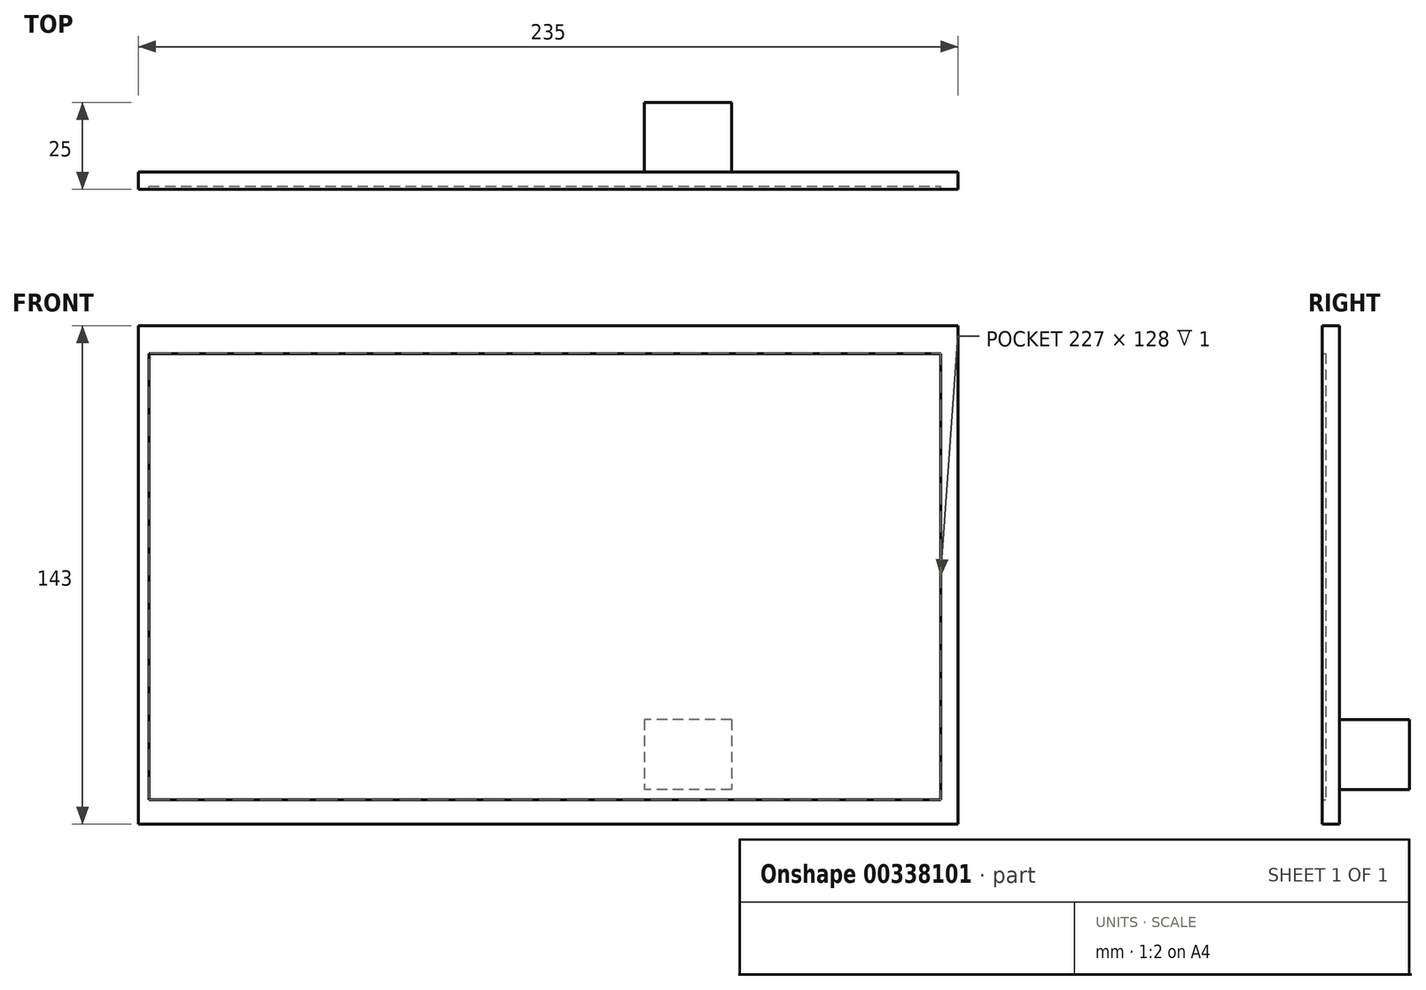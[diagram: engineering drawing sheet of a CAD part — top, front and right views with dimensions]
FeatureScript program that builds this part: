
annotation { "Feature Type Name" : "Feature", "Feature Type Description" : "" }
export const myFeature = defineFeature(function(context is Context, id is Id, definition is map)
    precondition{}
    {
        {
            var Q0;
            Q0=qCreatedBy(makeId("Front.planeOp"),FACE);
            var sketch = newSketch(context, id + "F0", { "sketchPlane" : qUnion([Q0])});
            skLineSegment(sketch, "E0.bottom", {"start": v(0, 0) * mm, "end": v(235, 0) * mm});
            skLineSegment(sketch, "E0.top", {"start": v(0, 143) * mm, "end": v(235, 143) * mm});
            skLineSegment(sketch, "E0.left", {"start": v(0, 0) * mm, "end": v(0, 143) * mm});
            skLineSegment(sketch, "E0.right", {"start": v(235, 0) * mm, "end": v(235, 143) * mm});
            skLineSegment(sketch, "E1.bottom", {"start": v(3, 135) * mm, "end": v(230, 135) * mm});
            skLineSegment(sketch, "E1.top", {"start": v(3, 7) * mm, "end": v(230, 7) * mm});
            skLineSegment(sketch, "E1.left", {"start": v(3, 135) * mm, "end": v(3, 7) * mm});
            skLineSegment(sketch, "E1.right", {"start": v(230, 135) * mm, "end": v(230, 7) * mm});
            skSolve(sketch);
        }
        {
            var Q0;
            Q0 = qSketchRegion(id + "F0", true);
            extrude(context, id + "F1", {"entities" : qUnion([Q0]), "depth" : 5 * mm});
        }
        {
            var Q0;
            Q0=qCreatedBy(makeId("Front.planeOp"),FACE);
            var sketch = newSketch(context, id + "F2", { "sketchPlane" : qUnion([Q0])});
            skLineSegment(sketch, "E2.0", {"start": v(3, 135) * mm, "end": v(230, 135) * mm});
            skLineSegment(sketch, "E2.1", {"start": v(3, 135) * mm, "end": v(3, 7) * mm});
            skLineSegment(sketch, "E2.2", {"start": v(3, 7) * mm, "end": v(230, 7) * mm});
            skLineSegment(sketch, "E2.3", {"start": v(230, 135) * mm, "end": v(230, 7) * mm});
            skSolve(sketch);
        }
        {
            var Q0;
            Q0=makeQuery(id+"F2.imprint","IMPRINT",FACE,{"disambiguationData":[TD([[makeQuery(id+"F2.imprint","IMPRINT",EDGE,{"derivedFrom":sQuery(id+"F2.wireOp",EDGE,"E2.0")}),-1.0]])]});
            extrude(context, id + "F3", {"entities" : qUnion([Q0]), "operationType" : NewBodyOperationType.ADD, "depth" : 4 * mm});
        }
        {
            var Q0;
            Q0=makeQuery(id+"F3.boolean.opBoolean","MERGE",FACE,{"derivedFrom":[makeQuery(id+"F1.opExtrude","CAP_FACE",FACE,{"disambiguationData":[OSD([sQuery(id+"F0.wireOp",EDGE,"E0.bottom"),sQuery(id+"F0.wireOp",EDGE,"E0.top"),sQuery(id+"F0.wireOp",EDGE,"E0.left"),sQuery(id+"F0.wireOp",EDGE,"E0.right"),sQuery(id+"F0.wireOp",EDGE,"E1.bottom"),sQuery(id+"F0.wireOp",EDGE,"E1.top"),sQuery(id+"F0.wireOp",EDGE,"E1.left"),sQuery(id+"F0.wireOp",EDGE,"E1.right")])],"isStart":true}),makeQuery(id+"F3.opExtrude","CAP_FACE",FACE,{"disambiguationData":[OSD([sQuery(id+"F2.wireOp",EDGE,"E2.0"),sQuery(id+"F2.wireOp",EDGE,"E2.1"),sQuery(id+"F2.wireOp",EDGE,"E2.2"),sQuery(id+"F2.wireOp",EDGE,"E2.3")])],"isStart":true})]});
            var sketch = newSketch(context, id + "F4", { "sketchPlane" : qUnion([Q0])});
            skLineSegment(sketch, "E3", {"start": v(-235, 30) * mm, "end": v(-170, 30) * mm, "construction": true});
            skLineSegment(sketch, "E4", {"start": v(-170, 0) * mm, "end": v(-170, 30) * mm, "construction": true});
            skLineSegment(sketch, "E5.bottom", {"start": v(-170, 30) * mm, "end": v(-145, 30) * mm});
            skLineSegment(sketch, "E5.top", {"start": v(-170, 10) * mm, "end": v(-145, 10) * mm});
            skLineSegment(sketch, "E5.left", {"start": v(-170, 30) * mm, "end": v(-170, 10) * mm});
            skLineSegment(sketch, "E5.right", {"start": v(-145, 30) * mm, "end": v(-145, 10) * mm});
            skSolve(sketch);
        }
        {
            var Q0;
            Q0=makeQuery(id+"F4.imprint","IMPRINT",FACE,{"disambiguationData":[TD([[makeQuery(id+"F4.imprint","IMPRINT",EDGE,{"derivedFrom":sQuery(id+"F4.wireOp",EDGE,"E5.bottom")}),-1.0]])]});
            extrude(context, id + "F5", {"entities" : qUnion([Q0]), "operationType" : NewBodyOperationType.ADD, "depth" : 20 * mm});
        }
    });
